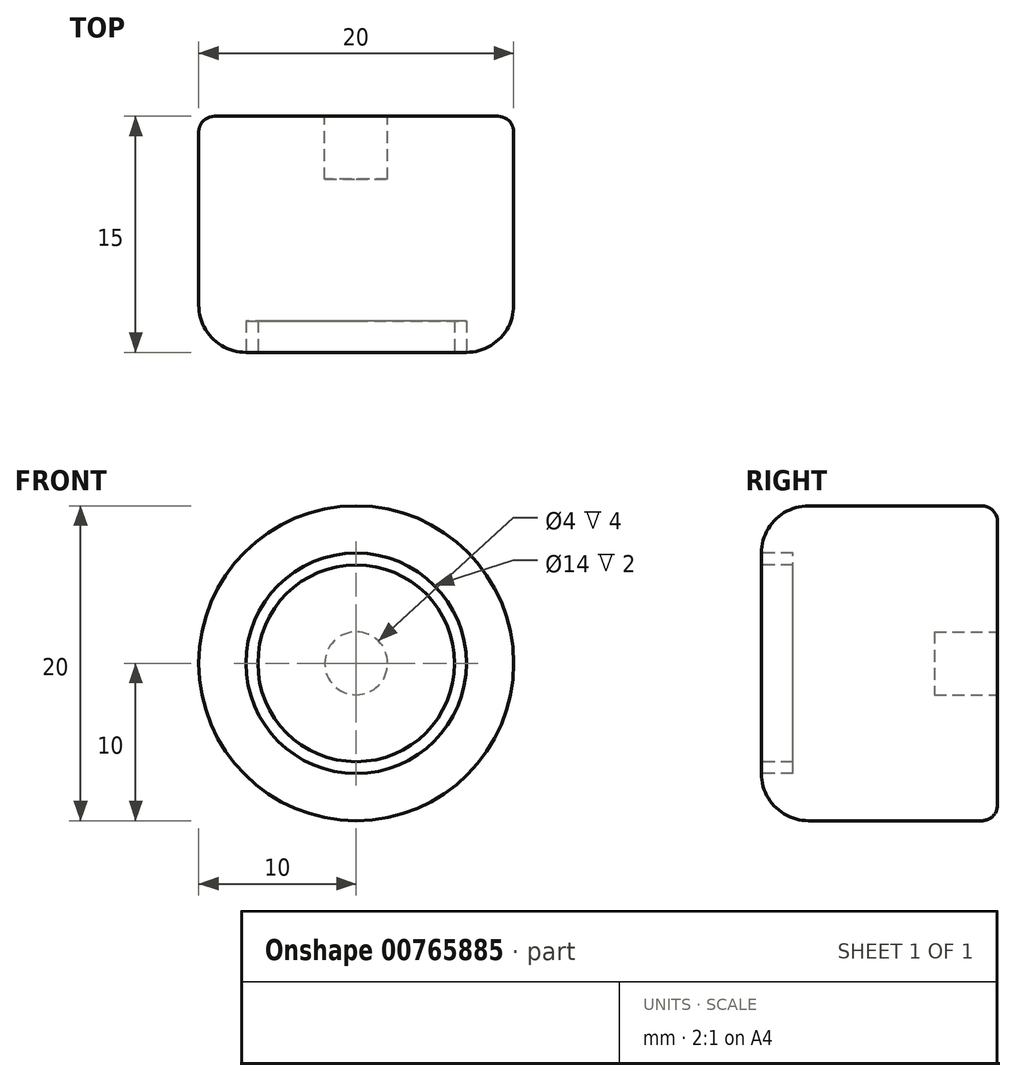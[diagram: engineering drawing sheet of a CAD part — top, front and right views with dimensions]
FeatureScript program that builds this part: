
annotation { "Feature Type Name" : "Feature", "Feature Type Description" : "" }
export const myFeature = defineFeature(function(context is Context, id is Id, definition is map)
    precondition{}
    {
        {
            var Q0;
            Q0=qCreatedBy(makeId("Front.planeOp"),FACE);
            var sketch = newSketch(context, id + "F0", { "sketchPlane" : qUnion([Q0])});
            skCircle(sketch, "E0", {"center": v(0, 0) * mm, "radius": 10 * mm});
            skSolve(sketch);
        }
        {
            var Q0;
            Q0=makeQuery(id+"F0.imprint","IMPRINT",FACE,{"disambiguationData":[TD([[makeQuery(id+"F0.imprint","IMPRINT",EDGE,{"derivedFrom":sQuery(id+"F0.wireOp",EDGE,"E0")}),1.0]])]});
            extrude(context, id + "F1", {"entities" : qUnion([Q0]), "depth" : 15 * mm, "offsetDistance" : 25 * mm});
        }
        {
            var Q0;
            Q0=makeQuery(id+"F1.opExtrude","CAP_FACE",FACE,{"disambiguationData":[OSD([sQuery(id+"F0.wireOp",EDGE,"E0")])],"isStart":false});
            fillet(context, id + "F2", {"entities" : qUnion([Q0]), "radius" : 3 * mm, "tangentPropagation" : true, "allowEdgeOverflow" : false});
        }
        {
            var Q0;
            Q0=makeQuery(id+"F1.opExtrude","CAP_EDGE",EDGE,{"disambiguationData":[OSD([sQuery(id+"F0.wireOp",EDGE,"E0")])],"isStart":true});
            fillet(context, id + "F3", {"entities" : qUnion([Q0]), "radius" : 1 * mm, "tangentPropagation" : true, "allowEdgeOverflow" : false});
        }
        {
            var Q0;
            Q0=makeQuery(id+"F1.opExtrude","CAP_FACE",FACE,{"disambiguationData":[OSD([sQuery(id+"F0.wireOp",EDGE,"E0")])],"isStart":true});
            var sketch = newSketch(context, id + "F4", { "sketchPlane" : qUnion([Q0])});
            skCircle(sketch, "E1", {"center": v(0, 0) * mm, "radius": 2 * mm});
            skSolve(sketch);
        }
        {
            var Q0;
            Q0 = qSketchRegion(id + "F4", true);
            extrude(context, id + "F5", {"entities" : qUnion([Q0]), "operationType" : NewBodyOperationType.REMOVE, "oppositeDirection" : true, "depth" : 4 * mm, "offsetDistance" : 25 * mm});
        }
        {
            var Q0;
            Q0=makeQuery(id+"F1.opExtrude","CAP_FACE",FACE,{"disambiguationData":[OSD([sQuery(id+"F0.wireOp",EDGE,"E0")])],"isStart":false});
            var sketch = newSketch(context, id + "F6", { "sketchPlane" : qUnion([Q0])});
            skCircle(sketch, "E2.0", {"center": v(0, 0) * mm, "radius": 6.25 * mm});
            skSolve(sketch);
        }
        {
            var Q0;
            Q0=makeQuery(id+"F6.imprint","IMPRINT",FACE,{"disambiguationData":[TD([[makeQuery(id+"F6.imprint","IMPRINT",EDGE,{"derivedFrom":sQuery(id+"F6.wireOp",EDGE,"E2.0")}),-1.0]])]});
            var sketch = newSketch(context, id + "F7", { "sketchPlane" : qUnion([Q0])});
            skSolve(sketch);
        }
        {
            var Q0;
            Q0 = qSketchRegion(id + "F7", true);
            var Q1;
            Q1=makeQuery(id+"F6.imprint","IMPRINT",FACE,{"disambiguationData":[TD([[makeQuery(id+"F6.imprint","IMPRINT",EDGE,{"derivedFrom":sQuery(id+"F6.wireOp",EDGE,"E2.0")}),-1.0]])]});
            extrude(context, id + "F8", {"entities" : qUnion([Q0, Q1]), "operationType" : NewBodyOperationType.REMOVE, "oppositeDirection" : true, "depth" : 2 * mm, "offsetDistance" : 25 * mm});
        }
    });
